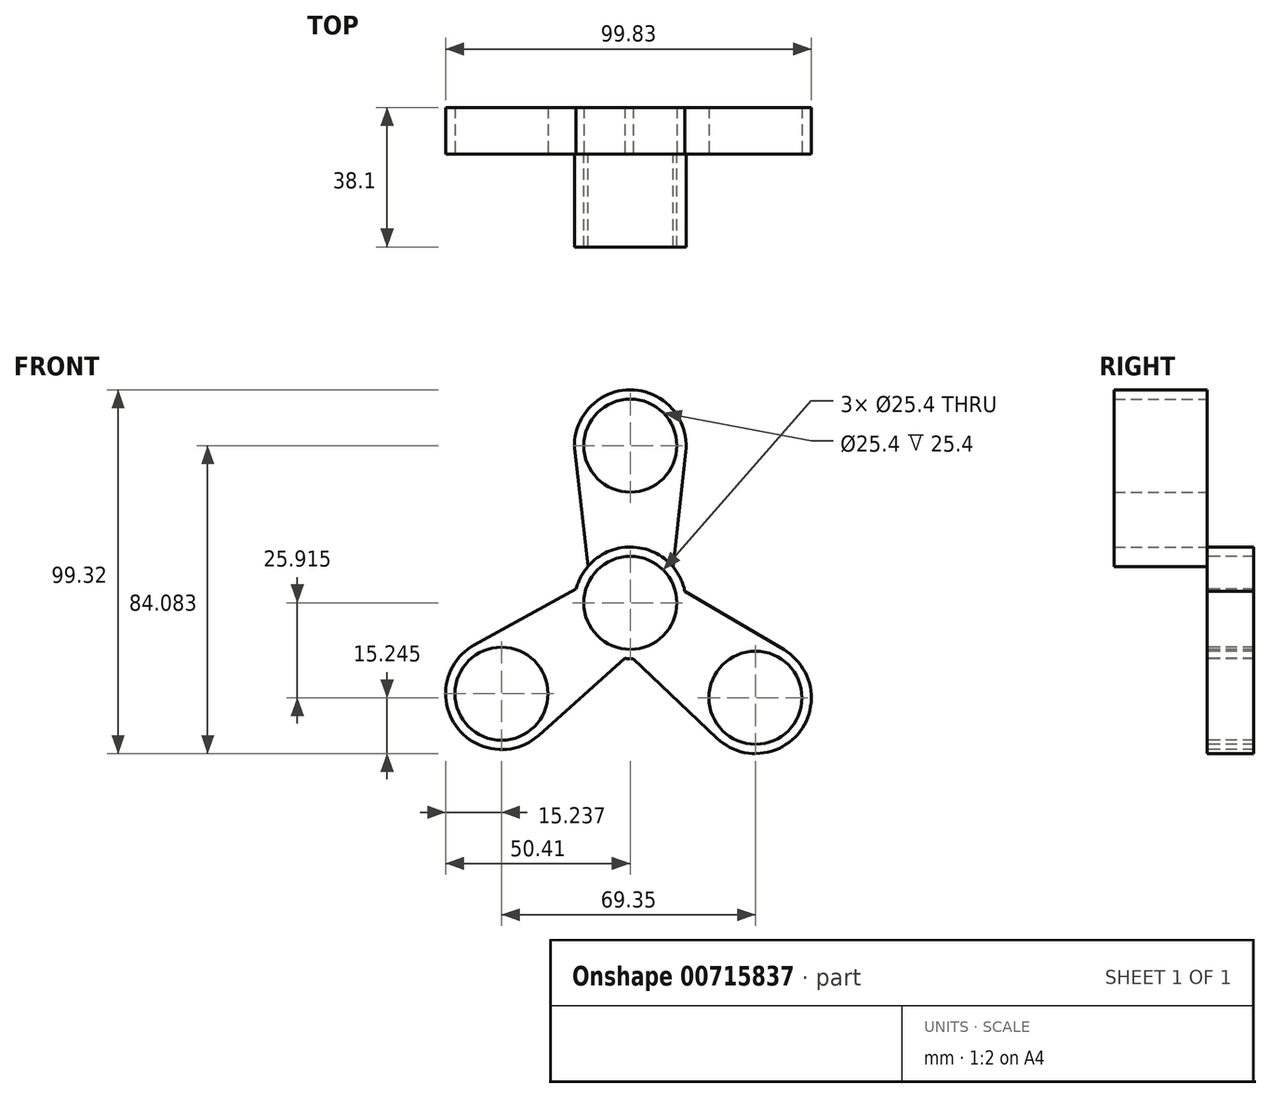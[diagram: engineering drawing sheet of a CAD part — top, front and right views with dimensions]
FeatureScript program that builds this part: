
annotation { "Feature Type Name" : "Feature", "Feature Type Description" : "" }
export const myFeature = defineFeature(function(context is Context, id is Id, definition is map)
    precondition{}
    {
        {
            var Q0;
            Q0=qCreatedBy(makeId("Front.planeOp"),FACE);
            var sketch = newSketch(context, id + "F0", { "sketchPlane" : qUnion([Q0])});
            skCircle(sketch, "E0", {"center": v(0, 0) * mm, "radius": 12.7 * mm});
            skCircle(sketch, "E1", {"center": v(0, 0) * mm, "radius": 15.24 * mm});
            skSolve(sketch);
        }
        {
            var Q0;
            Q0 = qSketchRegion(id + "F0", true);
            extrude(context, id + "F1", {"entities" : qUnion([Q0]), "oppositeDirection" : true, "depth" : 12.7 * mm, "offsetDistance" : 25.4 * mm});
        }
        {
            var Q0;
            Q0=qCreatedBy(makeId("Front.planeOp"),FACE);
            var sketch = newSketch(context, id + "F2", { "sketchPlane" : qUnion([Q0])});
            skCircle(sketch, "E2", {"center": v(0, 42.92) * mm, "radius": 12.7 * mm});
            skCircle(sketch, "E3", {"center": v(0, 42.92) * mm, "radius": 15.24 * mm});
            skCircle(sketch, "E4.0.0", {"center": v(0, 0) * mm, "radius": 15.24 * mm});
            skLineSegment(sketch, "E5", {"start": v(-15.14, 41.16) * mm, "end": v(-11.5, 10) * mm});
            skLineSegment(sketch, "E6", {"start": v(15.15, 41.24) * mm, "end": v(11.65, 9.83) * mm});
            skSolve(sketch);
        }
        {
            var Q0;
            {var subQ0=sQuery(id+"F2.wireOp",EDGE,"E5");Q0=makeQuery(id+"F2.imprint","IMPRINT",FACE,{"disambiguationData":[TD([[makeQuery(id+"F2.imprint","IMPRINT",EDGE,{"derivedFrom":subQ0}),1.0]])]});}
            var Q1;
            Q1=makeQuery(id+"F2.imprint","IMPRINT",FACE,{"disambiguationData":[TD([[makeQuery(id+"F2.imprint","IMPRINT",EDGE,{"derivedFrom":sQuery(id+"F2.wireOp",EDGE,"E2")}),-1.0]])]});
            extrude(context, id + "F3", {"entities" : qUnion([Q0, Q1]), "depth" : 25.4 * mm, "offsetDistance" : 25.4 * mm});
        }
        {
            var Q0;
            Q0=qCreatedBy(makeId("Front.planeOp"),FACE);
            var sketch = newSketch(context, id + "F4", { "sketchPlane" : qUnion([Q0])});
            skCircle(sketch, "E7", {"center": v(34.18, -25.92) * mm, "radius": 12.7 * mm});
            skCircle(sketch, "E8", {"center": v(34.18, -25.92) * mm, "radius": 15.24 * mm});
            skCircle(sketch, "E9.0", {"center": v(0, 0) * mm, "radius": 15.24 * mm});
            skLineSegment(sketch, "E10", {"start": v(41.91, -12.78) * mm, "end": v(14.92, 3.12) * mm});
            skLineSegment(sketch, "E11", {"start": v(23.69, -36.97) * mm, "end": v(0.77, -15.22) * mm});
            skCircle(sketch, "E12", {"center": v(-35.17, -24.81) * mm, "radius": 12.7 * mm});
            skCircle(sketch, "E13", {"center": v(-35.17, -24.81) * mm, "radius": 15.24 * mm});
            skLineSegment(sketch, "E14", {"start": v(-42.5, -11.45) * mm, "end": v(-14.78, 3.73) * mm});
            skLineSegment(sketch, "E15", {"start": v(-1.44, -15.17) * mm, "end": v(-25.03, -36.2) * mm});
            skSolve(sketch);
        }
        {
            var Q0;
            {var subQ0=sQuery(id+"F4.wireOp",EDGE,"E14");Q0=makeQuery(id+"F4.imprint","IMPRINT",FACE,{"disambiguationData":[TD([[makeQuery(id+"F4.imprint","IMPRINT",EDGE,{"derivedFrom":subQ0}),-1.0]])]});}
            var Q1;
            Q1=makeQuery(id+"F4.imprint","IMPRINT",FACE,{"disambiguationData":[TD([[makeQuery(id+"F4.imprint","IMPRINT",EDGE,{"derivedFrom":sQuery(id+"F4.wireOp",EDGE,"E12")}),-1.0]])]});
            var Q2;
            {var subQ0=sQuery(id+"F4.wireOp",EDGE,"E10");Q2=makeQuery(id+"F4.imprint","IMPRINT",FACE,{"disambiguationData":[TD([[makeQuery(id+"F4.imprint","IMPRINT",EDGE,{"derivedFrom":subQ0}),1.0]])]});}
            var Q3;
            Q3=makeQuery(id+"F4.imprint","IMPRINT",FACE,{"disambiguationData":[TD([[makeQuery(id+"F4.imprint","IMPRINT",EDGE,{"derivedFrom":sQuery(id+"F4.wireOp",EDGE,"E7")}),-1.0]])]});
            extrude(context, id + "F5", {"entities" : qUnion([Q0, Q1, Q2, Q3]), "operationType" : NewBodyOperationType.ADD, "oppositeDirection" : true, "depth" : 12.7 * mm, "offsetDistance" : 25.4 * mm});
        }
    });
